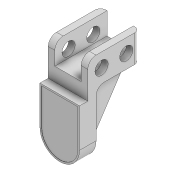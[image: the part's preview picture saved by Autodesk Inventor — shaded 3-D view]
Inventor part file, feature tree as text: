
AUTODESK INVENTOR PART (.ipt)
format: ipt  version: 2020.3 (Build 243373010, 373A)  size: 201,728 bytes
history: native  units: mm
features: extrude x6, sketch x6, projected_geometry x3, fillet x2, delete_face x1
ambient origin geometry x8: Origin, YZ Plane, XZ Plane, XY Plane, X Axis, Y Axis, Z Axis, Center Point
bodies: Solid1 (feature_tree)
feature tree (18):
  extrude  "Extrusion1"  Depth=36.0mm
  extrude  "Extrusion2"  Depth=7.5mm
  extrude  "Extrusion3"  Depth=25.0mm
  delete_face  "Delete Face1"
  fillet  "Fillet1"  Radius=15.0mm
  extrude  "Extrusion5"  Depth=36.0mm TaperAngle=0.0deg
  extrude  "Extrusion6"  Depth=20.0mm
  fillet  "Fillet2"  Radius=24.0mm
  extrude  "Extrusion7"  Depth=12.5mm TaperAngle=0.0deg
  sketch  "Sketch1"  dims[d0=36.0mm d2=35.0mm]
  sketch  "Sketch2"  dims[d3=15.0mm d4=0.0mm d8=7.5mm]
  sketch  "Sketch3"  dims[d10=40.0mm d11=25.0mm d12=15.0mm]
  sketch  "Sketch5"  dims[d13=36.0mm d14=0.0mm d15=15.0mm d16=0.0mm]
  projected_geometry  "Projected Loop3"
  sketch  "Sketch6"  dims[d17=2.0mm d21=20.0mm d22=24.0mm d23=0.0mm]
  projected_geometry  "Projected Loop4"
  sketch  "Sketch7"  dims[d24=1.5mm d25=0.25mm d26=0.0mm d27=5.0mm d28=25.0mm d29=12.0mm d30=47.5mm d31=12.5mm d32=12.0mm d33=12.5mm d34=0.0mm d35=0.0mm]
  projected_geometry  "Projected Loop5"
